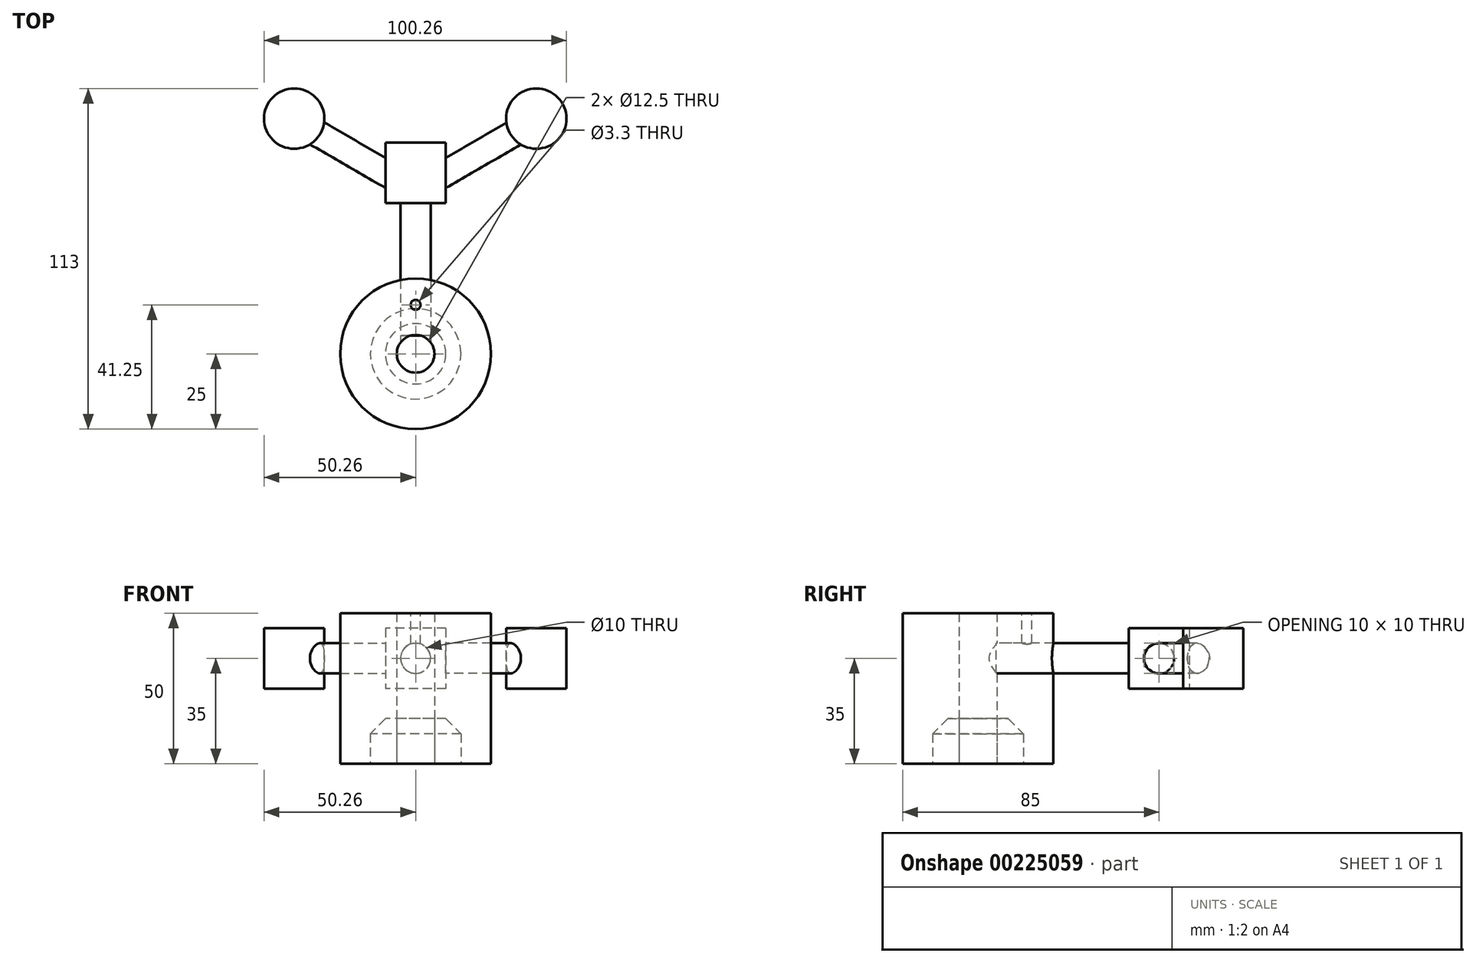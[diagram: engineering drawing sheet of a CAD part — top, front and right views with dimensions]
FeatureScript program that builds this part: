
annotation { "Feature Type Name" : "Feature", "Feature Type Description" : "" }
export const myFeature = defineFeature(function(context is Context, id is Id, definition is map)
    precondition{}
    {
        {
            var Q0;
            Q0=qCreatedBy(makeId("Top.planeOp"),FACE);
            var sketch = newSketch(context, id + "F0", { "sketchPlane" : qUnion([Q0])});
            skCircle(sketch, "E0", {"center": v(0, 0) * mm, "radius": 25 * mm});
            skCircle(sketch, "E1", {"center": v(0, 0) * mm, "radius": 6.25 * mm});
            skSolve(sketch);
        }
        {
            var Q0;
            Q0=qSketchRegion(id+"F0",true);
            extrude(context, id + "F1", {"entities" : qUnion([Q0]), "depth" : 50 * mm});
        }
        {
            var Q0;
            Q0=qCreatedBy(makeId("Front.planeOp"),FACE);
            var sketch = newSketch(context, id + "F2", { "sketchPlane" : qUnion([Q0])});
            skCircle(sketch, "E2", {"center": v(0, 35) * mm, "radius": 5 * mm});
            skSolve(sketch);
        }
        {
            var Q0;
            Q0=qSketchRegion(id+"F2",true);
            extrude(context, id + "F3", {"entities" : qUnion([Q0]), "operationType" : NewBodyOperationType.REMOVE, "oppositeDirection" : true, "depth" : 25 * mm});
        }
        {
            var Q0;
            Q0=makeQuery(id+"F1.opExtrude","CAP_FACE",FACE,{"disambiguationData":[OSD([sQuery(id+"F0.wireOp",EDGE,"E0"),sQuery(id+"F0.wireOp",EDGE,"E1")])],"isStart":false});
            var sketch = newSketch(context, id + "F4", { "sketchPlane" : qUnion([Q0])});
            skPoint(sketch, "E3", {"position": v(0, 16.25) * mm});
            skSolve(sketch);
        }
        {
            var Q0;
            Q0=sQuery(id+"F4.wireOp",VERTEX,"E3");
            var Q1;
            Q1=makeQuery(id+"F1.opExtrude","SWEPT_BODY",BODY,{"disambiguationData":[OSD([sQuery(id+"F0.wireOp",EDGE,"E0"),sQuery(id+"F0.wireOp",EDGE,"E1")])]});
            hole(context, id + "F5", {"style" : HoleStyle.SIMPLE, "endStyle" : HoleEndStyle.BLIND, "standardTappedOrClearance" : lookupTablePath({ "standard" : "ISO", "fit" : "Normal", "size" : "M3", "type" : "Clearance" }), "standardBlindInLast" : lookupTablePath({ "fit" : "Standard", "standard" : "ISO", "size" : "M3", "type" : "Clearance" }), "holeDiameter" : 3.3 * mm, "holeDepth" : 12 * mm, "locations" : qUnion([Q0]), "scope" : qUnion([Q1])});
        }
        {
            var Q0;
            Q0=qCreatedBy(makeId("Front.planeOp"),FACE);
            var sketch = newSketch(context, id + "F6", { "sketchPlane" : qUnion([Q0])});
            skCircle(sketch, "E4", {"center": v(0, 35) * mm, "radius": 5 * mm});
            skSolve(sketch);
        }
        {
            var Q0;
            Q0=qSketchRegion(id+"F6",true);
            var Q1;
            Q1=makeQuery(id+"F3.boolean.opBoolean","COPY",FACE,{"derivedFrom":makeQuery(id+"F3.opExtrude","SWEPT_FACE",FACE,{"disambiguationData":[OSD([sQuery(id+"F2.wireOp",EDGE,"E2")])]})});
            var Q2;
            Q2=makeQuery(id+"F1.opExtrude","SWEPT_BODY",BODY,{"disambiguationData":[OSD([sQuery(id+"F0.wireOp",EDGE,"E0"),sQuery(id+"F0.wireOp",EDGE,"E1")])]});
            extrude(context, id + "F7", {"entities" : qUnion([Q0]), "oppositeDirection" : true, "endBoundEntityFace" : qUnion([Q1]), "endBoundEntityBody" : qUnion([Q2]), "depth" : 50 * mm, "hasSecondDirection" : true, "secondDirectionOppositeDirection" : true, "secondDirectionDepth" : 6 * mm});
        }
        {
            var Q0;
            Q0=makeQuery(id+"F7.opExtrude","CAP_FACE",FACE,{"disambiguationData":[OSD([sQuery(id+"F6.wireOp",EDGE,"E4")])],"isStart":false});
            var sketch = newSketch(context, id + "F8", { "sketchPlane" : qUnion([Q0])});
            skLineSegment(sketch, "E5.bottom", {"start": v(-10, 45) * mm, "end": v(10, 45) * mm});
            skLineSegment(sketch, "E5.top", {"start": v(-10, 25) * mm, "end": v(10, 25) * mm});
            skLineSegment(sketch, "E5.left", {"start": v(-10, 45) * mm, "end": v(-10, 25) * mm});
            skLineSegment(sketch, "E5.right", {"start": v(10, 45) * mm, "end": v(10, 25) * mm});
            skSolve(sketch);
        }
        {
            var Q0;
            Q0=qSketchRegion(id+"F8",true);
            extrude(context, id + "F9", {"entities" : qUnion([Q0]), "operationType" : NewBodyOperationType.ADD, "depth" : 20 * mm});
        }
        {
            var Q0;
            Q0=makeQuery(id+"F9.opExtrude","SWEPT_FACE",FACE,{"disambiguationData":[OSD([sQuery(id+"F8.wireOp",EDGE,"E5.bottom")])]});
            var sketch = newSketch(context, id + "F10", { "sketchPlane" : qUnion([Q0])});
            skLineSegment(sketch, "E6", {"start": v(10, 60) * mm, "end": v(40, 77.32) * mm});
            skSolve(sketch);
        }
        {
            var Q0;
            {var subQ0=sQuery(id+"F8.wireOp",EDGE,"E5.bottom");var subQ1=makeQuery(id+"F9.opExtrude","CAP_EDGE",EDGE,{"disambiguationData":[OSD([subQ0])],"isStart":true});Q0=makeQuery(id+"F10.imprint","IMPRINT",FACE,{"disambiguationData":[TD([[makeQuery(id+"F10.imprint","IMPRINT",EDGE,{"derivedFrom":subQ1}),-1.0]])]});}
            var sketch = newSketch(context, id + "F11", { "sketchPlane" : qUnion([Q0])});
            skLineSegment(sketch, "E7", {"start": v(-9.95, 60) * mm, "end": v(-40, 77.35) * mm});
            skSolve(sketch);
        }
        {
            var Q0;
            Q0=makeQuery(id+"F9.opExtrude","SWEPT_FACE",FACE,{"disambiguationData":[OSD([sQuery(id+"F8.wireOp",EDGE,"E5.right")])]});
            var sketch = newSketch(context, id + "F12", { "sketchPlane" : qUnion([Q0])});
            skCircle(sketch, "E8", {"center": v(-60, 35) * mm, "radius": 5 * mm});
            skPoint(sketch, "E8.centerSnap0", {"position": v(-60, 25) * mm});
            skPoint(sketch, "E8.centerSnap1", {"position": v(-50, 35) * mm});
            skSolve(sketch);
        }
        {
            var Q0;
            Q0=makeQuery(id+"F9.opExtrude","SWEPT_FACE",FACE,{"disambiguationData":[OSD([sQuery(id+"F8.wireOp",EDGE,"E5.left")])]});
            var sketch = newSketch(context, id + "F13", { "sketchPlane" : qUnion([Q0])});
            skCircle(sketch, "E9", {"center": v(60, 35) * mm, "radius": 5 * mm});
            skPoint(sketch, "E9.centerSnap0", {"position": v(60, 25) * mm});
            skPoint(sketch, "E9.centerSnap1", {"position": v(50, 35) * mm});
            skSolve(sketch);
        }
        {
            var Q0;
            Q0=makeQuery(id+"F13.imprint","IMPRINT",FACE,{"disambiguationData":[TD([[makeQuery(id+"F13.imprint","IMPRINT",EDGE,{"derivedFrom":sQuery(id+"F13.wireOp",EDGE,"E9")}),1.0]])]});
            var Q1;
            Q1=sQuery(id+"F10.wireOp",EDGE,"E6");
            sweep(context, id + "F14", {"operationType" : NewBodyOperationType.ADD, "profiles" : qUnion([Q0]), "path" : qUnion([Q1])});
        }
        {
            var Q0;
            Q0=makeQuery(id+"F12.imprint","IMPRINT",FACE,{"disambiguationData":[TD([[makeQuery(id+"F12.imprint","IMPRINT",EDGE,{"derivedFrom":sQuery(id+"F12.wireOp",EDGE,"E8")}),1.0]])]});
            var Q1;
            Q1=sQuery(id+"F11.wireOp",EDGE,"E7");
            sweep(context, id + "F15", {"operationType" : NewBodyOperationType.ADD, "profiles" : qUnion([Q0]), "path" : qUnion([Q1])});
        }
        {
            var Q0;
            Q0=makeQuery(id+"F9.opExtrude","SWEPT_FACE",FACE,{"disambiguationData":[OSD([sQuery(id+"F8.wireOp",EDGE,"E5.bottom")])]});
            var sketch = newSketch(context, id + "F16", { "sketchPlane" : qUnion([Q0])});
            skCircle(sketch, "E10", {"center": v(40, 78) * mm, "radius": 10 * mm});
            skCircle(sketch, "E11", {"center": v(-40.26, 78) * mm, "radius": 10 * mm});
            skSolve(sketch);
        }
        {
            var Q0;
            Q0=qSketchRegion(id+"F16",true);
            extrude(context, id + "F17", {"entities" : qUnion([Q0]), "operationType" : NewBodyOperationType.ADD, "oppositeDirection" : true, "depth" : 20 * mm});
        }
        {
            var Q0;
            Q0=qCreatedBy(makeId("Top.planeOp"),FACE);
            var sketch = newSketch(context, id + "F18", { "sketchPlane" : qUnion([Q0])});
            skCircle(sketch, "E12", {"center": v(0, 0) * mm, "radius": 15 * mm});
            skCircle(sketch, "E13", {"center": v(0, 0) * mm, "radius": 6.25 * mm});
            skSolve(sketch);
        }
        {
            var Q0;
            Q0 = qSketchRegion(id + "F18", true);
            extrude(context, id + "F19", {"entities" : qUnion([Q0]), "depth" : 15 * mm});
        }
        {
            var Q0;
            Q0=makeQuery(id+"F19.opExtrude","CAP_EDGE",EDGE,{"disambiguationData":[OSD([sQuery(id+"F18.wireOp",EDGE,"E12")])],"isStart":false});
            chamfer(context, id + "F20", {"entities" : qUnion([Q0]), "width" : 5 * mm, "tangentPropagation" : true});
        }
    });
